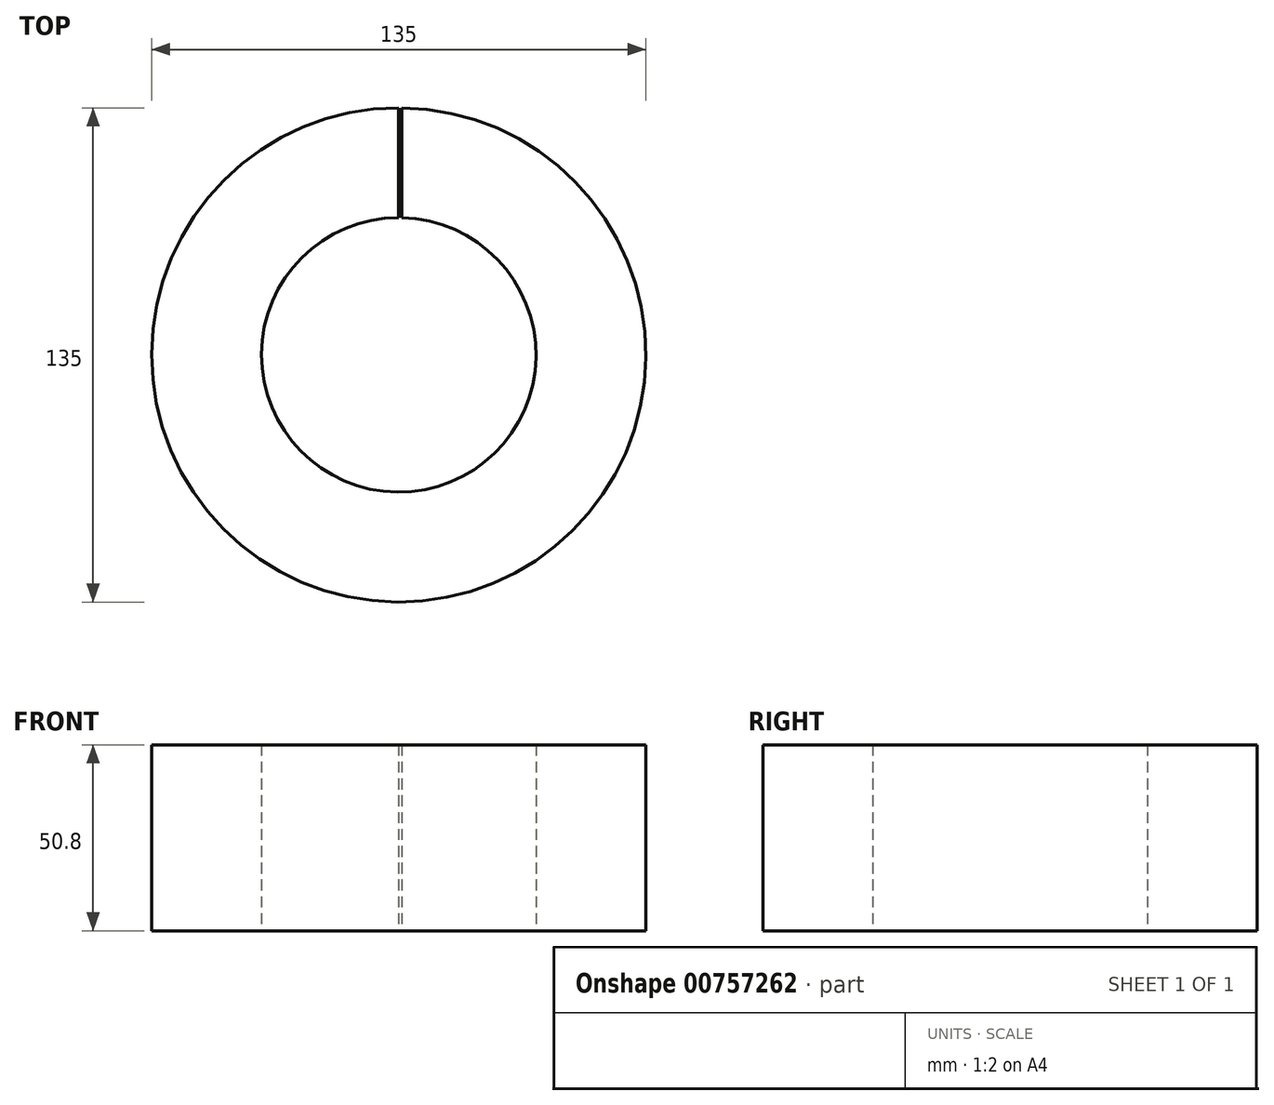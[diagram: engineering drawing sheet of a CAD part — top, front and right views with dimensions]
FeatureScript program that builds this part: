
annotation { "Feature Type Name" : "Feature", "Feature Type Description" : "" }
export const myFeature = defineFeature(function(context is Context, id is Id, definition is map)
    precondition{}
    {
        {
            var Q0;
            Q0=qCreatedBy(makeId("Top.planeOp"),FACE);
            var sketch = newSketch(context, id + "F0", { "sketchPlane" : qUnion([Q0])});
            skArc(sketch, "E0", {"start": v(0, 37.5) * mm, "mid": v(-0.38, -37.5) * mm, "end": v(0.76, 37.5) * mm});
            skArc(sketch, "E1", {"start": v(0, 67.5) * mm, "mid": v(-0.38, -67.5) * mm, "end": v(0.76, 67.5) * mm});
            skLineSegment(sketch, "E2", {"start": v(0, 37.5) * mm, "end": v(0, 67.5) * mm});
            skLineSegment(sketch, "E3", {"start": v(0.76, 37.5) * mm, "end": v(0.76, 67.5) * mm});
            skSolve(sketch);
        }
        {
            var Q0;
            Q0=makeQuery(id+"F0.imprint","IMPRINT",FACE,{"disambiguationData":[TD([[makeQuery(id+"F0.imprint","IMPRINT",EDGE,{"derivedFrom":sQuery(id+"F0.wireOp",EDGE,"E0")}),-1.0]])]});
            extrude(context, id + "F1", {"entities" : qUnion([Q0]), "depth" : 50.8 * mm, "offsetDistance" : 25.4 * mm});
        }
    });
